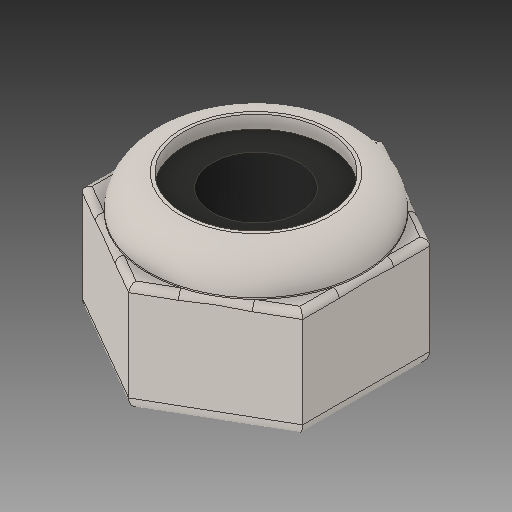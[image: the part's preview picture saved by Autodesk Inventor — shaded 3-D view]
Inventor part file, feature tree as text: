
AUTODESK INVENTOR PART (.ipt)
format: ipt  version: 2017 (Build 210142000, 142)  size: 228,352 bytes
history: native  units: in
note: dims shown in document units (in); Inventor stores cm internally (conversion verified against a paired STEP export)
features: fillet x1
ambient origin geometry x8: Origin, YZ Plane, XZ Plane, XY Plane, X Axis, Y Axis, Z Axis, Center Point
bodies: Solid1 (feature_tree)
feature tree (1):
  fillet  "Fillet6"  [1 undecoded]
note: 1 required parameter value undecoded (feature->parameter linkage not recoverable at this tier; creation-order binding heuristic only, values carry confidence <= 0.55)
